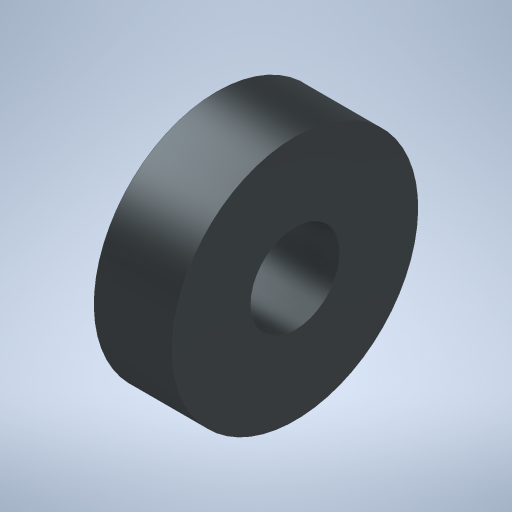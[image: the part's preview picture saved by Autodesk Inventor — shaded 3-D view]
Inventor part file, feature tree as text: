
AUTODESK INVENTOR PART (.ipt)
format: ipt  version: 2023 (Build 270158000, 158)  size: 235,520 bytes
history: native  units: mm
features: extrude x2, sketch x2, plane x1
ambient origin geometry x8: Origin, YZ Plane, XZ Plane, XY Plane, X Axis, Y Axis, Z Axis, Center Point
bodies: Volumenkörper1 (feature_tree)
feature tree (5):
  extrude  "Extrusion1"  Depth=7.0mm TaperAngle=0.0deg
  extrude  "Extrusion2"  TaperAngle=0.0deg  [1 undecoded]
  plane  "Arbeitsebene1"
  sketch  "Skizze1"  dims[d0=22.0mm d1=7.0mm d2=0.0mm]
  sketch  "Skizze2"  dims[d3=8.0mm d4=0.0mm d5=0.0mm d6=0.0mm]
note: 1 required parameter value undecoded (feature->parameter linkage not recoverable at this tier; creation-order binding heuristic only, values carry confidence <= 0.55)
